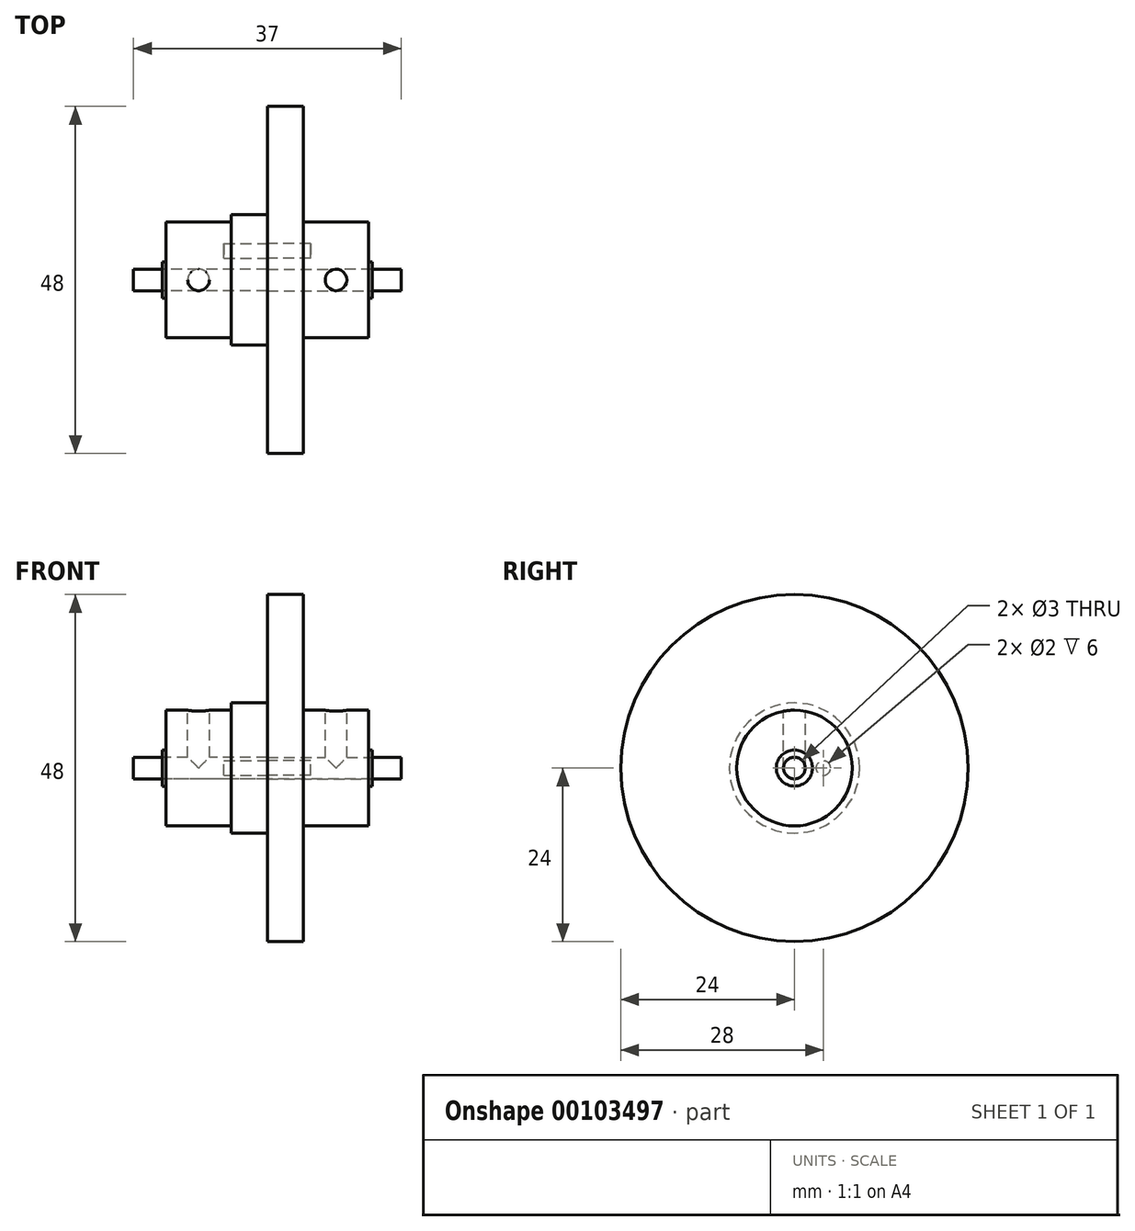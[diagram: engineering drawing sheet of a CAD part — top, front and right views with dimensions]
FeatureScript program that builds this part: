
annotation { "Feature Type Name" : "Feature", "Feature Type Description" : "" }
export const myFeature = defineFeature(function(context is Context, id is Id, definition is map)
    precondition{}
    {
        {
            var Q0;
            Q0=qCreatedBy(makeId("Front.planeOp"),FACE);
            var sketch = newSketch(context, id + "F0", { "sketchPlane" : qUnion([Q0])});
            skLineSegment(sketch, "E0", {"start": v(0, 0) * mm, "end": v(0, 24) * mm});
            skLineSegment(sketch, "E1", {"start": v(0, 24) * mm, "end": v(5, 24) * mm});
            skLineSegment(sketch, "E2", {"start": v(5, 24) * mm, "end": v(5, 8) * mm});
            skLineSegment(sketch, "E3", {"start": v(5, 8) * mm, "end": v(14, 8) * mm});
            skLineSegment(sketch, "E4", {"start": v(14, 8) * mm, "end": v(14, 2.5) * mm});
            skLineSegment(sketch, "E5", {"start": v(14, 2.5) * mm, "end": v(14.5, 2.5) * mm});
            skLineSegment(sketch, "E6", {"start": v(14.5, 2.5) * mm, "end": v(14.5, 0) * mm});
            skLineSegment(sketch, "E7", {"start": v(14.5, 0) * mm, "end": v(0, 0) * mm});
            skSolve(sketch);
        }
        {
            var Q0;
            Q0 = qSketchRegion(id + "F0", true);
            var Q1;
            Q1=sQuery(id+"F0.wireOp",EDGE,"E7");
            revolve(context, id + "F1", {"entities" : qUnion([Q0]), "axis" : qUnion([Q1]), "revolveType" : RevolveType.FULL});
        }
        {
            var Q0;
            Q0=sQuery(id+"F0.wireOp",VERTEX,"E4.start");
            var Q1;
            Q1=sQuery(id+"F0.wireOp",EDGE,"E0");
            cPlane(context, id + "F2", {"entities" : qUnion([Q0, Q1]), "cplaneType" : CPlaneType.LINE_POINT, "offset" : 150 * mm, "width" : 150 * mm, "height" : 150 * mm});
        }
        {
            var Q0;
            Q0=qCreatedBy(id+"F2.planeOp",FACE);
            var sketch = newSketch(context, id + "F3", { "sketchPlane" : qUnion([Q0])});
            skCircle(sketch, "E8", {"center": v(9.5, 0) * mm, "radius": 1.5 * mm});
            skSolve(sketch);
        }
        {
            var Q0;
            Q0=makeQuery(id+"F3.imprint","IMPRINT",FACE,{"disambiguationData":[TD([[makeQuery(id+"F3.imprint","IMPRINT",EDGE,{"derivedFrom":sQuery(id+"F3.wireOp",EDGE,"E8")}),1.0]])]});
            extrude(context, id + "F4", {"entities" : qUnion([Q0]), "operationType" : NewBodyOperationType.REMOVE, "oppositeDirection" : true, "depth" : 8 * mm});
        }
        {
            var Q0;
            Q0=makeQuery(id+"F1.opRevolve","SWEPT_FACE",FACE,{"disambiguationData":[OSD([sQuery(id+"F0.wireOp",EDGE,"E6")])]});
            var sketch = newSketch(context, id + "F5", { "sketchPlane" : qUnion([Q0])});
            skCircle(sketch, "E9", {"center": v(0, 0) * mm, "radius": 1.5 * mm});
            skSolve(sketch);
        }
        {
            var Q0;
            Q0=makeQuery(id+"F5.imprint","IMPRINT",FACE,{"disambiguationData":[TD([[makeQuery(id+"F5.imprint","IMPRINT",EDGE,{"derivedFrom":sQuery(id+"F5.wireOp",EDGE,"E9")}),1.0]])]});
            extrude(context, id + "F6", {"entities" : qUnion([Q0]), "operationType" : NewBodyOperationType.REMOVE, "endBound" : BoundingType.THROUGH_ALL, "oppositeDirection" : true, "depth" : 25 * mm});
        }
        {
            var Q0;
            Q0=qCreatedBy(makeId("Front.planeOp"),FACE);
            var sketch = newSketch(context, id + "F7", { "sketchPlane" : qUnion([Q0])});
            skLineSegment(sketch, "E10", {"start": v(0, 0) * mm, "end": v(0, 9) * mm});
            skLineSegment(sketch, "E11", {"start": v(0, 9) * mm, "end": v(-5, 9) * mm});
            skLineSegment(sketch, "E12", {"start": v(-5, 9) * mm, "end": v(-5, 8) * mm});
            skLineSegment(sketch, "E13", {"start": v(-5, 8) * mm, "end": v(-14, 8) * mm});
            skLineSegment(sketch, "E14", {"start": v(-14, 8) * mm, "end": v(-14, 2.5) * mm});
            skLineSegment(sketch, "E15", {"start": v(-14, 2.5) * mm, "end": v(-14.5, 2.5) * mm});
            skLineSegment(sketch, "E16", {"start": v(-14.5, 2.5) * mm, "end": v(-14.5, 0) * mm});
            skLineSegment(sketch, "E17", {"start": v(-14.5, 0) * mm, "end": v(0, 0) * mm});
            skSolve(sketch);
        }
        {
            var Q0;
            Q0=makeQuery(id+"F7.imprint","IMPRINT",FACE,{"disambiguationData":[TD([[makeQuery(id+"F7.imprint","IMPRINT",EDGE,{"derivedFrom":sQuery(id+"F7.wireOp",EDGE,"E10")}),1.0]])]});
            var Q1;
            Q1=sQuery(id+"F7.wireOp",EDGE,"E17");
            revolve(context, id + "F8", {"entities" : qUnion([Q0]), "axis" : qUnion([Q1]), "revolveType" : RevolveType.FULL});
        }
        {
            var Q0;
            Q0=qCreatedBy(id+"F2.planeOp",FACE);
            var sketch = newSketch(context, id + "F9", { "sketchPlane" : qUnion([Q0])});
            skCircle(sketch, "E18", {"center": v(-9.5, 0) * mm, "radius": 1.5 * mm});
            skSolve(sketch);
        }
        {
            var Q0;
            Q0=makeQuery(id+"F9.imprint","IMPRINT",FACE,{"disambiguationData":[TD([[makeQuery(id+"F9.imprint","IMPRINT",EDGE,{"derivedFrom":sQuery(id+"F9.wireOp",EDGE,"E18")}),1.0]])]});
            extrude(context, id + "F10", {"entities" : qUnion([Q0]), "operationType" : NewBodyOperationType.REMOVE, "oppositeDirection" : true, "depth" : 8 * mm});
        }
        {
            var Q0;
            Q0=makeQuery(id+"F8.opRevolve","SWEPT_FACE",FACE,{"disambiguationData":[OSD([sQuery(id+"F7.wireOp",EDGE,"E16")])]});
            var sketch = newSketch(context, id + "F11", { "sketchPlane" : qUnion([Q0])});
            skCircle(sketch, "E19", {"center": v(0, 0) * mm, "radius": 1.5 * mm});
            skSolve(sketch);
        }
        {
            var Q0;
            Q0 = qSketchRegion(id + "F11", true);
            var Q1;
            Q1=makeQuery(id+"F8.opRevolve","SWEPT_FACE",FACE,{"disambiguationData":[OSD([sQuery(id+"F7.wireOp",EDGE,"E10")])]});
            extrude(context, id + "F12", {"entities" : qUnion([Q0]), "operationType" : NewBodyOperationType.REMOVE, "endBound" : BoundingType.UP_TO_SURFACE, "oppositeDirection" : true, "endBoundEntityFace" : qUnion([Q1]), "depth" : 25 * mm});
        }
        {
            var Q0;
            Q0=makeQuery(id+"F8.opRevolve","SWEPT_FACE",FACE,{"disambiguationData":[OSD([sQuery(id+"F7.wireOp",EDGE,"E10")])]});
            var sketch = newSketch(context, id + "F13", { "sketchPlane" : qUnion([Q0])});
            skCircle(sketch, "E20", {"center": v(4, 0) * mm, "radius": 1 * mm});
            skSolve(sketch);
        }
        {
            var Q0;
            Q0=makeQuery(id+"F13.imprint","IMPRINT",FACE,{"disambiguationData":[TD([[makeQuery(id+"F13.imprint","IMPRINT",EDGE,{"derivedFrom":sQuery(id+"F13.wireOp",EDGE,"E20")}),1.0]])]});
            extrude(context, id + "F14", {"entities" : qUnion([Q0]), "operationType" : NewBodyOperationType.REMOVE, "oppositeDirection" : true, "depth" : 6 * mm});
        }
        {
            var Q0;
            Q0=makeQuery(id+"F13.imprint","IMPRINT",FACE,{"disambiguationData":[TD([[makeQuery(id+"F13.imprint","IMPRINT",EDGE,{"derivedFrom":sQuery(id+"F13.wireOp",EDGE,"E20")}),1.0]])]});
            extrude(context, id + "F15", {"entities" : qUnion([Q0]), "operationType" : NewBodyOperationType.REMOVE, "depth" : 6 * mm});
        }
        {
            var Q0;
            Q0=qCreatedBy(makeId("Right.planeOp"),FACE);
            var sketch = newSketch(context, id + "F16", { "sketchPlane" : qUnion([Q0])});
            skCircle(sketch, "E21", {"center": v(0, 0) * mm, "radius": 1.5 * mm});
            skSolve(sketch);
        }
        {
            var Q0;
            Q0 = qSketchRegion(id + "F16", true);
            extrude(context, id + "F17", {"entities" : qUnion([Q0]), "endBound" : BoundingType.SYMMETRIC, "depth" : 37 * mm});
        }
    });
